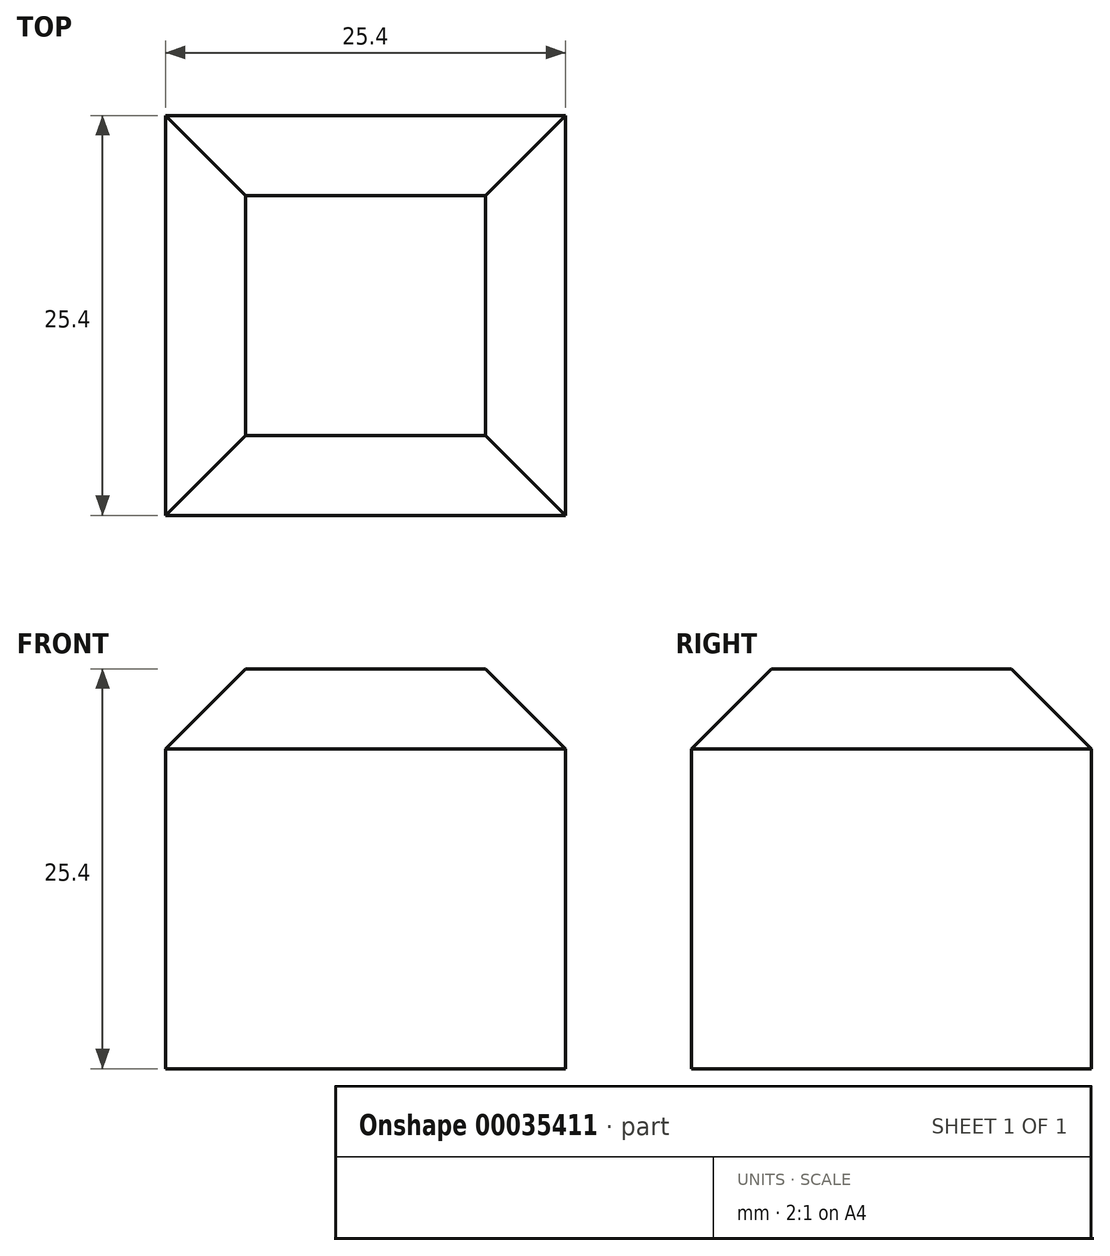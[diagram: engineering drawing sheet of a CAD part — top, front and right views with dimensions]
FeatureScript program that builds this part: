
annotation { "Feature Type Name" : "Feature", "Feature Type Description" : "" }
export const myFeature = defineFeature(function(context is Context, id is Id, definition is map)
    precondition{}
    {
        {
            var Q0;
            Q0=qCreatedBy(makeId("Top.planeOp"),FACE);
            var sketch = newSketch(context, id + "F0", { "sketchPlane" : qUnion([Q0])});
            skLineSegment(sketch, "E0.bottom", {"start": v(0, 0) * mm, "end": v(25.4, 0) * mm});
            skLineSegment(sketch, "E0.top", {"start": v(0, -25.4) * mm, "end": v(25.4, -25.4) * mm});
            skLineSegment(sketch, "E0.left", {"start": v(0, 0) * mm, "end": v(0, -25.4) * mm});
            skLineSegment(sketch, "E0.right", {"start": v(25.4, 0) * mm, "end": v(25.4, -25.4) * mm});
            skSolve(sketch);
        }
        {
            var Q0;
            Q0=makeQuery(id+"F0.imprint","IMPRINT",FACE,{"disambiguationData":[TD([[makeQuery(id+"F0.imprint","IMPRINT",EDGE,{"derivedFrom":sQuery(id+"F0.wireOp",EDGE,"E0.bottom")}),-1.0]])]});
            extrude(context, id + "F1", {"entities" : qUnion([Q0]), "depth" : 25.4 * mm});
        }
        {
            var Q0;
            Q0=makeQuery(id+"F1.opExtrude","CAP_EDGE",EDGE,{"disambiguationData":[OSD([sQuery(id+"F0.wireOp",EDGE,"E0.top")])],"isStart":false});
            var Q1;
            Q1=makeQuery(id+"F1.opExtrude","CAP_EDGE",EDGE,{"disambiguationData":[OSD([sQuery(id+"F0.wireOp",EDGE,"E0.right")])],"isStart":false});
            var Q2;
            Q2=makeQuery(id+"F1.opExtrude","CAP_EDGE",EDGE,{"disambiguationData":[OSD([sQuery(id+"F0.wireOp",EDGE,"E0.bottom")])],"isStart":false});
            var Q3;
            Q3=makeQuery(id+"F1.opExtrude","CAP_EDGE",EDGE,{"disambiguationData":[OSD([sQuery(id+"F0.wireOp",EDGE,"E0.left")])],"isStart":false});
            chamfer(context, id + "F2", {"entities" : qUnion([Q0, Q1, Q2, Q3]), "width" : 5.08 * mm, "tangentPropagation" : true});
        }
    });
